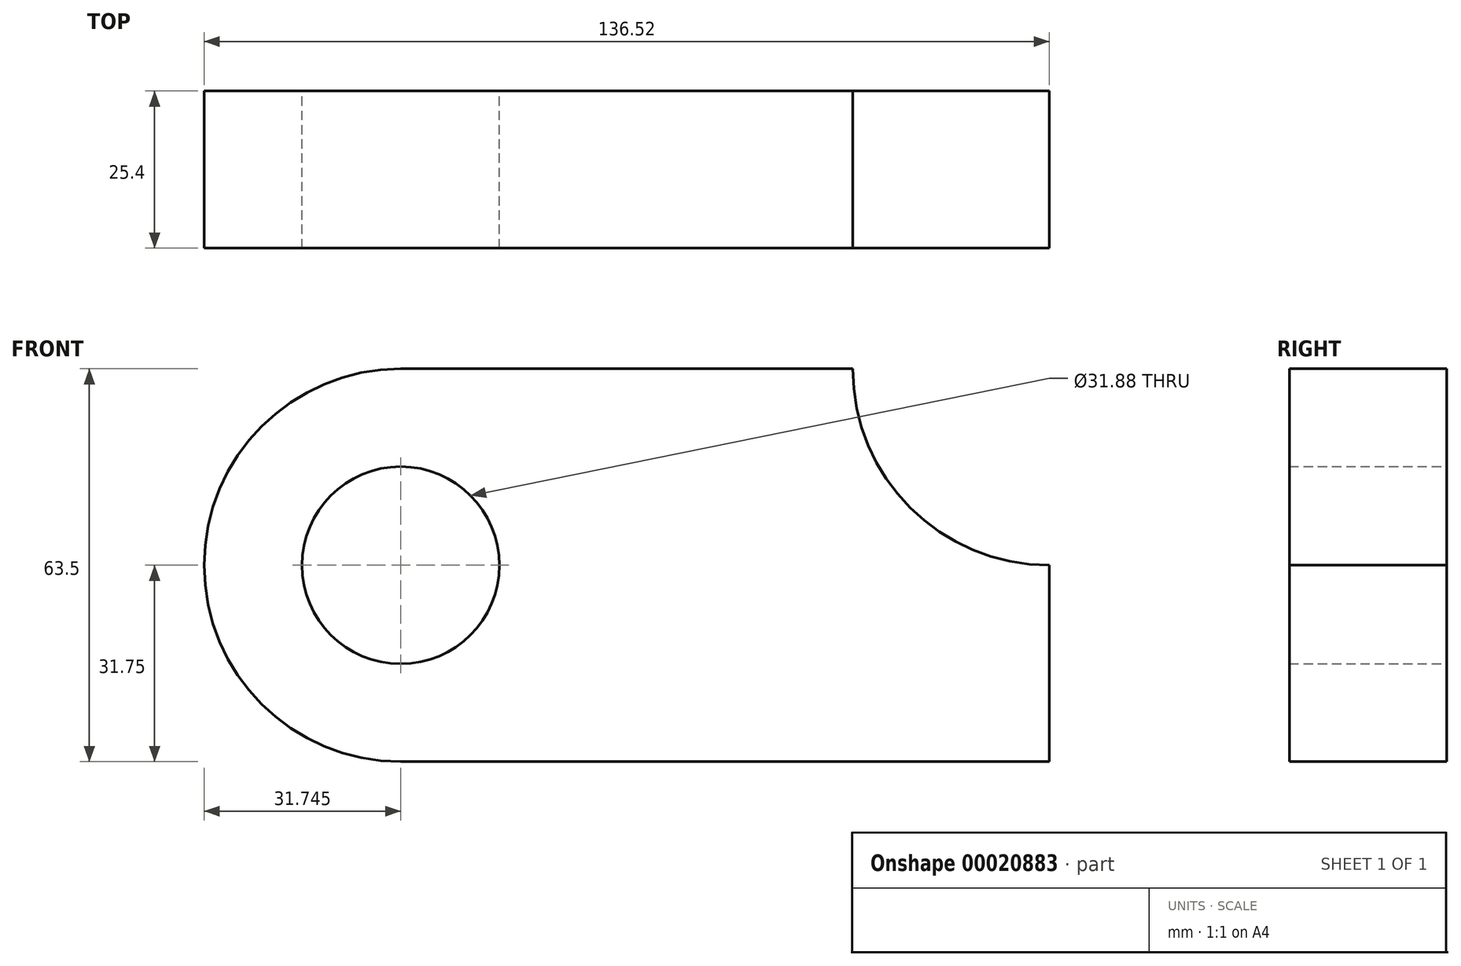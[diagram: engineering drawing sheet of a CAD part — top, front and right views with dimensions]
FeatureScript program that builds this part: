
annotation { "Feature Type Name" : "Feature", "Feature Type Description" : "" }
export const myFeature = defineFeature(function(context is Context, id is Id, definition is map)
    precondition{}
    {
        {
            var Q0;
            Q0=qCreatedBy(makeId("Front.planeOp"),FACE);
            var sketch = newSketch(context, id + "F0", { "sketchPlane" : qUnion([Q0])});
            skLineSegment(sketch, "E0.bottom", {"start": v(0, 0) * mm, "end": v(-104.78, 0) * mm});
            skLineSegment(sketch, "E0.top", {"start": v(-31.75, 63.5) * mm, "end": v(-104.78, 63.5) * mm});
            skLineSegment(sketch, "E0.left", {"start": v(0, 0) * mm, "end": v(0, 31.75) * mm});
            skLineSegment(sketch, "E0.right", {"start": v(-104.78, 0) * mm, "end": v(-104.78, 63.5) * mm});
            skCircle(sketch, "E1", {"center": v(-104.78, 31.75) * mm, "radius": 31.75 * mm});
            skCircle(sketch, "E2", {"center": v(-104.78, 31.75) * mm, "radius": 15.94 * mm});
            skArc(sketch, "E3", {"start": v(-31.75, 63.5) * mm, "mid": v(-22.45, 41.05) * mm, "end": v(0, 31.75) * mm});
            skSolve(sketch);
        }
        {
            var Q0;
            {var subQ3=sQuery(id+"F0.wireOp",EDGE,"E0.bottom");Q0=makeQuery(id+"F0.imprint","IMPRINT",FACE,{"disambiguationData":[TD([[makeQuery(id+"F0.imprint","IMPRINT",EDGE,{"derivedFrom":subQ3}),-1.0]])]});}
            var Q1;
            {var subQ0=sQuery(id+"F0.wireOp",EDGE,"E2");var subQ1=sQuery(id+"F0.wireOp",EDGE,"E0.right");var subQ3=makeQuery(id+"F0.imprint","INTERSECT",VERTEX,{"disambiguationData":[OD(0.0)],"derivedFrom":[subQ1,subQ0]});Q1=makeQuery(id+"F0.imprint","IMPRINT",FACE,{"disambiguationData":[TD([[makeQuery(id+"F0.imprint","IMPRINT",EDGE,{"disambiguationData":[TD([[subQ3,1.0]])],"derivedFrom":subQ0}),-1.0]])]});}
            var Q2;
            {var subQ0=sQuery(id+"F0.wireOp",EDGE,"E2");var subQ1=sQuery(id+"F0.wireOp",EDGE,"E0.right");var subQ3=makeQuery(id+"F0.imprint","INTERSECT",VERTEX,{"disambiguationData":[OD(0.0)],"derivedFrom":[subQ1,subQ0]});Q2=makeQuery(id+"F0.imprint","IMPRINT",FACE,{"disambiguationData":[TD([[makeQuery(id+"F0.imprint","IMPRINT",EDGE,{"disambiguationData":[TD([[subQ3,-1.0]])],"derivedFrom":subQ0}),-1.0]])]});}
            extrude(context, id + "F1", {"entities" : qUnion([Q0, Q1, Q2]), "depth" : 25.4 * mm});
        }
    });
